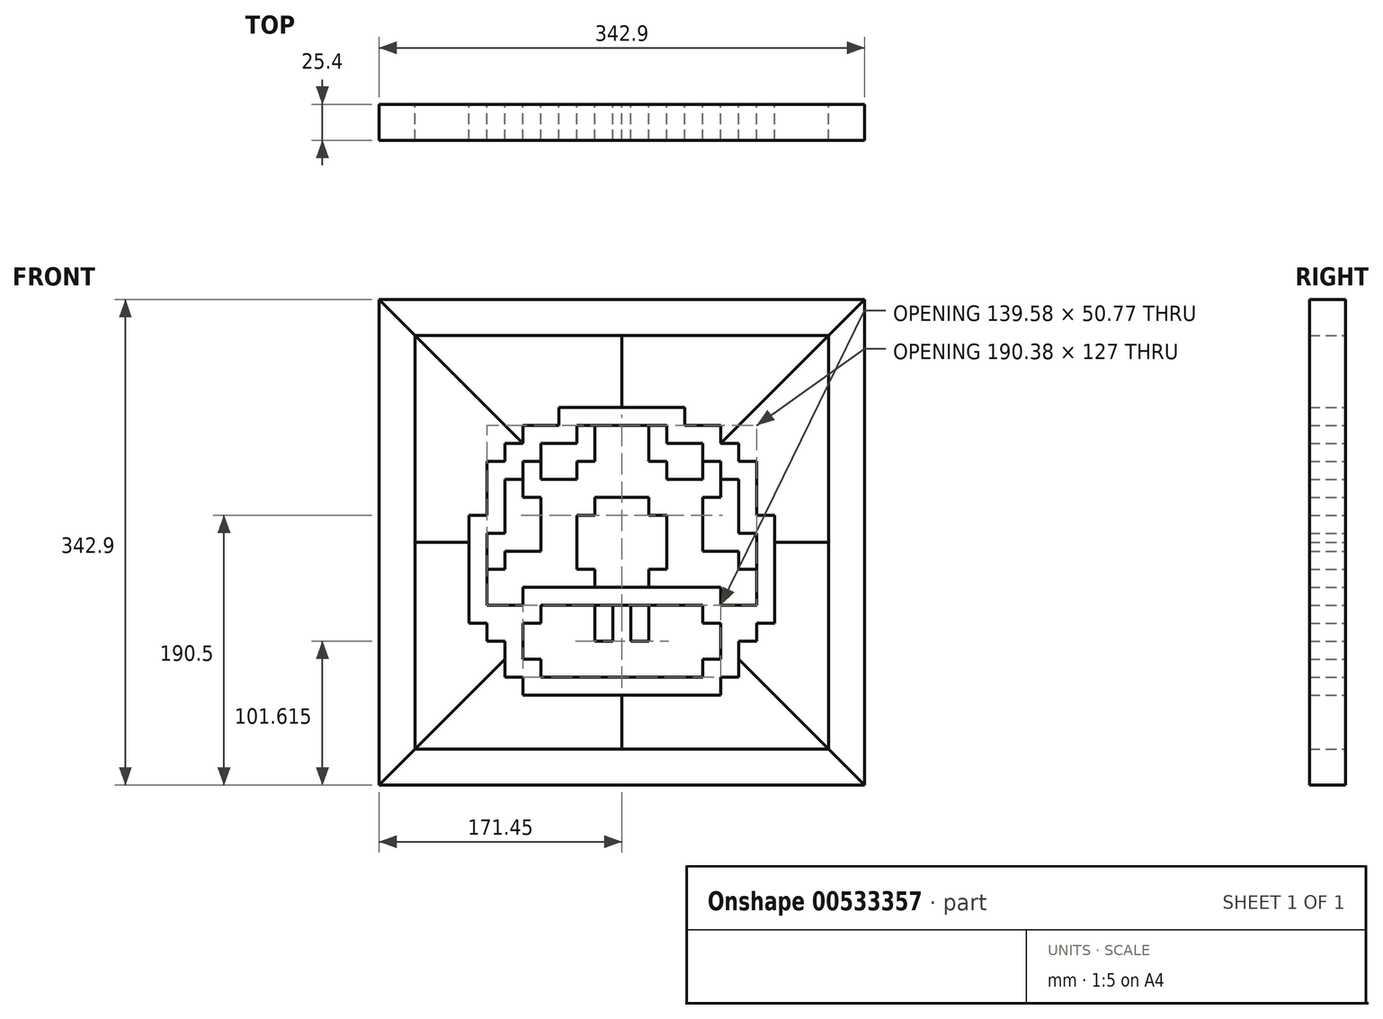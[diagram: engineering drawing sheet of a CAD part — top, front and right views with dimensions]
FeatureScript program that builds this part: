
annotation { "Feature Type Name" : "Feature", "Feature Type Description" : "" }
export const myFeature = defineFeature(function(context is Context, id is Id, definition is map)
    precondition{}
    {
        {
            var Q0;
            Q0=qCreatedBy(makeId("Front.planeOp"),FACE);
            var sketch = newSketch(context, id + "F0", { "sketchPlane" : qUnion([Q0])});
            skLineSegment(sketch, "E0.bottom", {"start": v(-171.45, 171.45) * mm, "end": v(171.45, 171.45) * mm});
            skLineSegment(sketch, "E0.top", {"start": v(-171.45, -171.45) * mm, "end": v(171.45, -171.45) * mm});
            skLineSegment(sketch, "E0.left", {"start": v(-171.45, 171.45) * mm, "end": v(-171.45, -171.45) * mm});
            skLineSegment(sketch, "E0.right", {"start": v(171.45, 171.45) * mm, "end": v(171.45, -171.45) * mm});
            skPoint(sketch, "E0.middle", {"position": v(0, 0) * mm});
            skLineSegment(sketch, "E1.0", {"start": v(-146.05, 146.05) * mm, "end": v(146.05, 146.05) * mm});
            skLineSegment(sketch, "E2.0", {"start": v(146.05, 146.05) * mm, "end": v(146.05, -146.05) * mm});
            skLineSegment(sketch, "E3.0", {"start": v(-146.05, -146.05) * mm, "end": v(146.05, -146.05) * mm});
            skLineSegment(sketch, "E4.0", {"start": v(-146.05, 146.05) * mm, "end": v(-146.05, -146.05) * mm});
            skLineSegment(sketch, "E5", {"start": v(-171.45, 171.45) * mm, "end": v(-146.05, 146.05) * mm});
            skLineSegment(sketch, "E6", {"start": v(171.45, 171.45) * mm, "end": v(146.05, 146.05) * mm});
            skLineSegment(sketch, "E7", {"start": v(171.45, -171.45) * mm, "end": v(146.05, -146.05) * mm});
            skLineSegment(sketch, "E8", {"start": v(-171.45, -171.45) * mm, "end": v(-146.05, -146.05) * mm});
            skLineSegment(sketch, "E9.top", {"start": v(-69.8, -107.92) * mm, "end": v(69.8, -107.92) * mm});
            skLineSegment(sketch, "E10", {"start": v(-69.8, -107.92) * mm, "end": v(-69.8, -95.22) * mm});
            skLineSegment(sketch, "E11", {"start": v(-57.1, -95.22) * mm, "end": v(0, -95.22) * mm});
            skLineSegment(sketch, "E12", {"start": v(-69.8, -95.22) * mm, "end": v(-82.5, -95.22) * mm});
            skLineSegment(sketch, "E13", {"start": v(-82.5, -95.22) * mm, "end": v(-82.5, -82.5) * mm});
            skLineSegment(sketch, "E14", {"start": v(-82.5, -69.82) * mm, "end": v(-95.2, -69.85) * mm});
            skLineSegment(sketch, "E15", {"start": v(-57.1, -82.55) * mm, "end": v(-69.8, -82.55) * mm});
            skLineSegment(sketch, "E16", {"start": v(-69.8, -82.55) * mm, "end": v(-69.8, -57.15) * mm});
            skLineSegment(sketch, "E17", {"start": v(-95.2, -69.85) * mm, "end": v(-95.2, -57.15) * mm});
            skLineSegment(sketch, "E18", {"start": v(-95.2, -57.15) * mm, "end": v(-107.9, -57.15) * mm});
            skLineSegment(sketch, "E19", {"start": v(-69.8, -57.15) * mm, "end": v(-57.1, -57.15) * mm});
            skLineSegment(sketch, "E20", {"start": v(-57.1, -57.15) * mm, "end": v(-57.1, -44.45) * mm});
            skLineSegment(sketch, "E21", {"start": v(-57.1, -44.45) * mm, "end": v(0, -44.45) * mm});
            skLineSegment(sketch, "E22", {"start": v(-107.9, -57.15) * mm, "end": v(-107.9, 19.05) * mm});
            skLineSegment(sketch, "E23", {"start": v(-107.9, 19.05) * mm, "end": v(-95.2, 19.05) * mm});
            skLineSegment(sketch, "E24", {"start": v(-95.2, 19.05) * mm, "end": v(-95.25, 57.15) * mm});
            skLineSegment(sketch, "E25", {"start": v(-95.25, 57.15) * mm, "end": v(-82.55, 57.15) * mm});
            skLineSegment(sketch, "E26", {"start": v(-82.55, 57.15) * mm, "end": v(-82.55, 69.85) * mm});
            skLineSegment(sketch, "E27", {"start": v(-82.55, 69.85) * mm, "end": v(-69.85, 69.85) * mm});
            skLineSegment(sketch, "E28", {"start": v(-69.85, 69.85) * mm, "end": v(-69.85, 82.55) * mm});
            skLineSegment(sketch, "E29", {"start": v(-69.85, 82.55) * mm, "end": v(-44.45, 82.55) * mm});
            skLineSegment(sketch, "E30", {"start": v(-44.45, 82.55) * mm, "end": v(-44.45, 95.25) * mm});
            skLineSegment(sketch, "E31", {"start": v(-44.45, 95.25) * mm, "end": v(0, 95.25) * mm});
            skLineSegment(sketch, "E32", {"start": v(-57.1, -82.55) * mm, "end": v(-57.1, -95.22) * mm});
            skLineSegment(sketch, "E33", {"start": v(-69.8, -44.45) * mm, "end": v(-95.2, -44.45) * mm});
            skLineSegment(sketch, "E34", {"start": v(-95.2, -44.45) * mm, "end": v(-95.2, 6.35) * mm});
            skLineSegment(sketch, "E35", {"start": v(-95.2, 6.35) * mm, "end": v(-82.5, 6.35) * mm});
            skLineSegment(sketch, "E36", {"start": v(-82.5, 6.35) * mm, "end": v(-82.5, 44.45) * mm});
            skLineSegment(sketch, "E37", {"start": v(-82.5, 44.45) * mm, "end": v(-69.8, 44.45) * mm});
            skLineSegment(sketch, "E38", {"start": v(-69.8, 44.45) * mm, "end": v(-69.8, 57.15) * mm});
            skLineSegment(sketch, "E39", {"start": v(-69.8, 57.15) * mm, "end": v(-57.1, 57.15) * mm});
            skLineSegment(sketch, "E40", {"start": v(-57.1, 57.15) * mm, "end": v(-57.1, 69.85) * mm});
            skLineSegment(sketch, "E41", {"start": v(-57.1, 69.85) * mm, "end": v(-31.7, 69.85) * mm});
            skLineSegment(sketch, "E42", {"start": v(-31.7, 69.85) * mm, "end": v(-31.7, 82.55) * mm});
            skLineSegment(sketch, "E43", {"start": v(-31.7, 82.55) * mm, "end": v(0, 82.55) * mm});
            skLineSegment(sketch, "E44", {"start": v(0, 100.28) * mm, "end": v(0, -44.45) * mm, "construction": true});
            skLineSegment(sketch, "E45.MirrorCS", {"start": v(95.2, -69.85) * mm, "end": v(95.2, -57.15) * mm});
            skLineSegment(sketch, "E46.MirrorCS", {"start": v(44.45, 82.55) * mm, "end": v(44.45, 95.25) * mm});
            skLineSegment(sketch, "E47.MirrorCS", {"start": v(82.5, -69.82) * mm, "end": v(95.2, -69.85) * mm});
            skLineSegment(sketch, "E48.MirrorCS", {"start": v(82.5, -95.22) * mm, "end": v(82.5, -69.82) * mm});
            skLineSegment(sketch, "E49.MirrorCS", {"start": v(69.85, 82.55) * mm, "end": v(44.45, 82.55) * mm});
            skLineSegment(sketch, "E50.MirrorCS", {"start": v(82.5, 44.45) * mm, "end": v(69.8, 44.45) * mm});
            skLineSegment(sketch, "E51.MirrorCS", {"start": v(107.9, -57.15) * mm, "end": v(107.9, 19.05) * mm});
            skLineSegment(sketch, "E52.MirrorCS", {"start": v(69.8, -107.92) * mm, "end": v(-69.8, -107.92) * mm});
            skLineSegment(sketch, "E53.MirrorCS", {"start": v(82.55, 57.15) * mm, "end": v(82.55, 69.85) * mm});
            skLineSegment(sketch, "E54.MirrorCS", {"start": v(82.5, 6.35) * mm, "end": v(82.5, 44.45) * mm});
            skLineSegment(sketch, "E55.MirrorCS", {"start": v(57.1, -57.15) * mm, "end": v(57.1, -44.45) * mm});
            skLineSegment(sketch, "E56.MirrorCS", {"start": v(95.2, -57.15) * mm, "end": v(107.9, -57.15) * mm});
            skLineSegment(sketch, "E57.MirrorCS", {"start": v(82.55, 69.85) * mm, "end": v(69.85, 69.85) * mm});
            skLineSegment(sketch, "E58.MirrorCS", {"start": v(31.7, 82.55) * mm, "end": v(0, 82.55) * mm});
            skLineSegment(sketch, "E59.MirrorCS", {"start": v(69.8, 44.45) * mm, "end": v(69.8, 57.15) * mm});
            skLineSegment(sketch, "E60.MirrorCS", {"start": v(57.1, -95.22) * mm, "end": v(0, -95.22) * mm});
            skLineSegment(sketch, "E61.MirrorCS", {"start": v(69.8, -107.92) * mm, "end": v(69.8, -95.22) * mm});
            skLineSegment(sketch, "E62.MirrorCS", {"start": v(69.8, -44.45) * mm, "end": v(95.2, -44.45) * mm});
            skLineSegment(sketch, "E63.MirrorCS", {"start": v(57.1, 57.15) * mm, "end": v(57.1, 69.85) * mm});
            skLineSegment(sketch, "E64.MirrorCS", {"start": v(69.8, -57.15) * mm, "end": v(57.1, -57.15) * mm});
            skLineSegment(sketch, "E65.MirrorCS", {"start": v(95.25, 57.15) * mm, "end": v(82.55, 57.15) * mm});
            skLineSegment(sketch, "E66.MirrorCS", {"start": v(95.2, -44.45) * mm, "end": v(95.2, 6.35) * mm});
            skLineSegment(sketch, "E67.MirrorCS", {"start": v(57.1, -82.55) * mm, "end": v(69.8, -82.55) * mm});
            skLineSegment(sketch, "E68.MirrorCS", {"start": v(69.8, 57.15) * mm, "end": v(57.1, 57.15) * mm});
            skLineSegment(sketch, "E69.MirrorCS", {"start": v(69.8, -95.22) * mm, "end": v(82.5, -95.22) * mm});
            skLineSegment(sketch, "E70.MirrorCS", {"start": v(95.2, 6.35) * mm, "end": v(82.5, 6.35) * mm});
            skLineSegment(sketch, "E71.MirrorCS", {"start": v(107.9, 19.05) * mm, "end": v(95.2, 19.05) * mm});
            skLineSegment(sketch, "E72.MirrorCS", {"start": v(44.45, 95.25) * mm, "end": v(0, 95.25) * mm});
            skLineSegment(sketch, "E73.MirrorCS", {"start": v(57.1, -44.45) * mm, "end": v(0, -44.45) * mm});
            skLineSegment(sketch, "E74.MirrorCS", {"start": v(31.7, 69.85) * mm, "end": v(31.7, 82.55) * mm});
            skLineSegment(sketch, "E75.MirrorCS", {"start": v(57.1, 69.85) * mm, "end": v(31.7, 69.85) * mm});
            skLineSegment(sketch, "E76.MirrorCS", {"start": v(69.85, 69.85) * mm, "end": v(69.85, 82.55) * mm});
            skLineSegment(sketch, "E77.MirrorCS", {"start": v(95.2, 19.05) * mm, "end": v(95.25, 57.15) * mm});
            skLineSegment(sketch, "E78.MirrorCS", {"start": v(69.8, -82.55) * mm, "end": v(69.8, -57.15) * mm});
            skLineSegment(sketch, "E79.MirrorCS", {"start": v(57.1, -82.55) * mm, "end": v(57.1, -95.22) * mm});
            skLineSegment(sketch, "E80", {"start": v(-19.05, -44.45) * mm, "end": v(-19.05, -69.85) * mm});
            skLineSegment(sketch, "E81", {"start": v(-19.05, -69.85) * mm, "end": v(-6.35, -69.85) * mm});
            skLineSegment(sketch, "E82", {"start": v(-6.35, -69.85) * mm, "end": v(-6.35, -44.45) * mm});
            skLineSegment(sketch, "E83.MirrorCS", {"start": v(19.05, -69.85) * mm, "end": v(6.35, -69.85) * mm});
            skLineSegment(sketch, "E84.MirrorCS", {"start": v(19.05, -44.45) * mm, "end": v(19.05, -69.85) * mm});
            skLineSegment(sketch, "E85.MirrorCS", {"start": v(6.35, -69.85) * mm, "end": v(6.35, -44.45) * mm});
            skLineSegment(sketch, "E86", {"start": v(-19.05, -31.75) * mm, "end": v(-19.05, -19.05) * mm});
            skLineSegment(sketch, "E87", {"start": v(-19.05, -19.05) * mm, "end": v(-31.75, -19.05) * mm});
            skLineSegment(sketch, "E88", {"start": v(-31.75, -19.05) * mm, "end": v(-31.75, 19.05) * mm});
            skLineSegment(sketch, "E89", {"start": v(-31.75, 19.05) * mm, "end": v(-19.05, 19.05) * mm});
            skLineSegment(sketch, "E90", {"start": v(-19.05, 19.05) * mm, "end": v(-19.05, 31.75) * mm});
            skLineSegment(sketch, "E91", {"start": v(-19.05, 31.75) * mm, "end": v(19.05, 31.75) * mm});
            skLineSegment(sketch, "E92", {"start": v(19.05, 31.75) * mm, "end": v(19.05, 19.05) * mm});
            skLineSegment(sketch, "E93", {"start": v(19.05, 19.05) * mm, "end": v(31.75, 19.05) * mm});
            skLineSegment(sketch, "E94", {"start": v(31.75, 19.05) * mm, "end": v(31.75, -19.05) * mm});
            skLineSegment(sketch, "E95", {"start": v(31.75, -19.05) * mm, "end": v(19.05, -19.05) * mm});
            skLineSegment(sketch, "E96", {"start": v(19.05, -19.05) * mm, "end": v(19.05, -31.75) * mm});
            skLineSegment(sketch, "E97", {"start": v(-95.2, -19.05) * mm, "end": v(-82.5, -19.05) * mm});
            skLineSegment(sketch, "E98", {"start": v(-82.5, -19.05) * mm, "end": v(-82.5, -6.35) * mm});
            skLineSegment(sketch, "E99", {"start": v(-82.5, -6.35) * mm, "end": v(-57.1, -6.35) * mm});
            skLineSegment(sketch, "E100", {"start": v(-57.1, -6.35) * mm, "end": v(-57.1, 31.75) * mm});
            skLineSegment(sketch, "E101", {"start": v(-57.1, 31.75) * mm, "end": v(-69.8, 31.75) * mm});
            skLineSegment(sketch, "E102", {"start": v(-69.8, 31.75) * mm, "end": v(-69.8, 44.45) * mm});
            skLineSegment(sketch, "E103", {"start": v(-57.1, 57.15) * mm, "end": v(-57.1, 44.45) * mm});
            skLineSegment(sketch, "E104", {"start": v(-57.1, 44.45) * mm, "end": v(-31.7, 44.45) * mm});
            skLineSegment(sketch, "E105", {"start": v(-31.7, 44.45) * mm, "end": v(-31.7, 57.15) * mm});
            skLineSegment(sketch, "E106", {"start": v(-31.7, 57.15) * mm, "end": v(-19, 57.15) * mm});
            skLineSegment(sketch, "E107", {"start": v(-19, 57.15) * mm, "end": v(-19, 82.55) * mm});
            skLineSegment(sketch, "E108.MirrorCS", {"start": v(19, 57.15) * mm, "end": v(19, 82.55) * mm});
            skLineSegment(sketch, "E109.MirrorCS", {"start": v(31.7, 57.15) * mm, "end": v(19, 57.15) * mm});
            skLineSegment(sketch, "E110.MirrorCS", {"start": v(31.7, 44.45) * mm, "end": v(31.7, 57.15) * mm});
            skLineSegment(sketch, "E111.MirrorCS", {"start": v(57.1, 44.45) * mm, "end": v(31.7, 44.45) * mm});
            skLineSegment(sketch, "E112.MirrorCS", {"start": v(57.1, 57.15) * mm, "end": v(57.1, 44.45) * mm});
            skLineSegment(sketch, "E113.MirrorCS", {"start": v(69.8, 31.75) * mm, "end": v(69.8, 44.45) * mm});
            skLineSegment(sketch, "E114.MirrorCS", {"start": v(57.1, -6.35) * mm, "end": v(57.1, 31.75) * mm});
            skLineSegment(sketch, "E115.MirrorCS", {"start": v(82.5, -6.35) * mm, "end": v(57.1, -6.35) * mm});
            skLineSegment(sketch, "E116.MirrorCS", {"start": v(82.5, -19.05) * mm, "end": v(82.5, -6.35) * mm});
            skLineSegment(sketch, "E117.MirrorCS", {"start": v(95.2, -19.05) * mm, "end": v(82.5, -19.05) * mm});
            skLineSegment(sketch, "E118.MirrorCS", {"start": v(57.1, 31.75) * mm, "end": v(69.8, 31.75) * mm});
            skLineSegment(sketch, "E119", {"start": v(-146.05, 146.05) * mm, "end": v(-69.85, 69.85) * mm});
            skLineSegment(sketch, "E120", {"start": v(0, 95.25) * mm, "end": v(0, 146.05) * mm});
            skLineSegment(sketch, "E121", {"start": v(146.05, 146.05) * mm, "end": v(69.85, 69.85) * mm});
            skLineSegment(sketch, "E122", {"start": v(-146.05, -146.05) * mm, "end": v(-82.5, -82.5) * mm});
            skLineSegment(sketch, "E123", {"start": v(-82.5, -82.5) * mm, "end": v(-82.5, -69.82) * mm});
            skLineSegment(sketch, "E124.MirrorCS", {"start": v(146.05, -146.05) * mm, "end": v(82.5, -82.5) * mm});
            skLineSegment(sketch, "E125", {"start": v(-107.9, 0) * mm, "end": v(-146.05, 0) * mm});
            skLineSegment(sketch, "E126.MirrorCS", {"start": v(107.9, 0) * mm, "end": v(146.05, 0) * mm});
            skLineSegment(sketch, "E127", {"start": v(0, -107.92) * mm, "end": v(0, -146.05) * mm});
            skLineSegment(sketch, "E128", {"start": v(-69.8, -44.45) * mm, "end": v(-69.8, -31.75) * mm});
            skLineSegment(sketch, "E129", {"start": v(-69.8, -31.75) * mm, "end": v(69.8, -31.75) * mm});
            skLineSegment(sketch, "E130", {"start": v(69.8, -31.75) * mm, "end": v(69.8, -44.45) * mm});
            skSolve(sketch);
        }
        {
            var Q0;
            Q0=makeQuery(id+"F0.imprint","IMPRINT",FACE,{"disambiguationData":[TD([[makeQuery(id+"F0.imprint","IMPRINT",EDGE,{"derivedFrom":sQuery(id+"F0.wireOp",EDGE,"E0.bottom")}),-1.0]])]});
            var Q1;
            Q1=makeQuery(id+"F0.imprint","IMPRINT",FACE,{"disambiguationData":[TD([[makeQuery(id+"F0.imprint","IMPRINT",EDGE,{"derivedFrom":sQuery(id+"F0.wireOp",EDGE,"E0.top")}),1.0]])]});
            var Q2;
            Q2=makeQuery(id+"F0.imprint","IMPRINT",FACE,{"disambiguationData":[TD([[makeQuery(id+"F0.imprint","IMPRINT",EDGE,{"derivedFrom":sQuery(id+"F0.wireOp",EDGE,"E14")}),1.0]])]});
            var Q3;
            Q3=makeQuery(id+"F0.imprint","IMPRINT",FACE,{"disambiguationData":[TD([[makeQuery(id+"F0.imprint","IMPRINT",EDGE,{"derivedFrom":sQuery(id+"F0.wireOp",EDGE,"E45.MirrorCS")}),-1.0]])]});
            extrude(context, id + "F1", {"entities" : qUnion([Q0, Q1, Q2, Q3]), "depth" : 25.4 * mm, "offsetDistance" : 25.4 * mm});
        }
        {
            var Q0;
            Q0=makeQuery(id+"F0.imprint","IMPRINT",FACE,{"disambiguationData":[TD([[makeQuery(id+"F0.imprint","IMPRINT",EDGE,{"derivedFrom":sQuery(id+"F0.wireOp",EDGE,"E0.left")}),1.0]])]});
            var Q1;
            Q1=makeQuery(id+"F0.imprint","IMPRINT",FACE,{"disambiguationData":[TD([[makeQuery(id+"F0.imprint","IMPRINT",EDGE,{"derivedFrom":sQuery(id+"F0.wireOp",EDGE,"E0.right")}),-1.0]])]});
            var Q2;
            {var subQ3=sQuery(id+"F0.wireOp",EDGE,"E10");Q2=makeQuery(id+"F0.imprint","IMPRINT",FACE,{"disambiguationData":[TD([[makeQuery(id+"F0.imprint","IMPRINT",EDGE,{"derivedFrom":subQ3}),1.0]])]});}
            var Q3;
            {var subQ0=sQuery(id+"F0.wireOp",EDGE,"E86");Q3=makeQuery(id+"F0.imprint","IMPRINT",FACE,{"disambiguationData":[TD([[makeQuery(id+"F0.imprint","IMPRINT",EDGE,{"derivedFrom":subQ0}),-1.0]])]});}
            extrude(context, id + "F2", {"entities" : qUnion([Q0, Q1, Q2, Q3]), "depth" : 25.4 * mm, "offsetDistance" : 25.4 * mm});
        }
        {
            var Q0;
            {var subQ0=sQuery(id+"F0.wireOp",EDGE,"E61.MirrorCS");Q0=makeQuery(id+"F0.imprint","IMPRINT",FACE,{"disambiguationData":[TD([[makeQuery(id+"F0.imprint","IMPRINT",EDGE,{"derivedFrom":subQ0}),-1.0]])]});}
            var Q1;
            {var subQ0=sQuery(id+"F0.wireOp",EDGE,"E23");Q1=makeQuery(id+"F0.imprint","IMPRINT",FACE,{"disambiguationData":[TD([[makeQuery(id+"F0.imprint","IMPRINT",EDGE,{"derivedFrom":subQ0}),1.0]])]});}
            var Q2;
            Q2=makeQuery(id+"F0.imprint","IMPRINT",FACE,{"disambiguationData":[TD([[makeQuery(id+"F0.imprint","IMPRINT",EDGE,{"derivedFrom":sQuery(id+"F0.wireOp",EDGE,"E46.MirrorCS")}),-1.0]])]});
            extrude(context, id + "F3", {"entities" : qUnion([Q0, Q1, Q2]), "depth" : 25.4 * mm, "offsetDistance" : 25.4 * mm});
        }
        {
            var Q0;
            Q0=makeQuery(id+"F0.imprint","IMPRINT",FACE,{"disambiguationData":[TD([[makeQuery(id+"F0.imprint","IMPRINT",EDGE,{"derivedFrom":sQuery(id+"F0.wireOp",EDGE,"E28")}),1.0]])]});
            var Q1;
            Q1=makeQuery(id+"F0.imprint","IMPRINT",FACE,{"disambiguationData":[TD([[makeQuery(id+"F0.imprint","IMPRINT",EDGE,{"derivedFrom":sQuery(id+"F0.wireOp",EDGE,"E53.MirrorCS")}),-1.0]])]});
            var Q2;
            {var subQ1=sQuery(id+"F0.wireOp",EDGE,"E33");Q2=makeQuery(id+"F0.imprint","IMPRINT",FACE,{"disambiguationData":[TD([[makeQuery(id+"F0.imprint","IMPRINT",EDGE,{"derivedFrom":subQ1}),-1.0]])]});}
            extrude(context, id + "F4", {"entities" : qUnion([Q0, Q1, Q2]), "depth" : 25.4 * mm, "offsetDistance" : 25.4 * mm});
        }
        {
            var Q0;
            {var subQ0=sQuery(id+"F0.wireOp",EDGE,"E80");Q0=makeQuery(id+"F0.imprint","IMPRINT",FACE,{"disambiguationData":[TD([[makeQuery(id+"F0.imprint","IMPRINT",EDGE,{"derivedFrom":subQ0}),1.0]])]});}
            var Q1;
            Q1=makeQuery(id+"F0.imprint","IMPRINT",FACE,{"disambiguationData":[TD([[makeQuery(id+"F0.imprint","IMPRINT",EDGE,{"derivedFrom":sQuery(id+"F0.wireOp",EDGE,"E83.MirrorCS")}),-1.0]])]});
            var Q2;
            Q2=makeQuery(id+"F0.imprint","IMPRINT",FACE,{"disambiguationData":[TD([[makeQuery(id+"F0.imprint","IMPRINT",EDGE,{"derivedFrom":sQuery(id+"F0.wireOp",EDGE,"E50.MirrorCS")}),1.0]])]});
            var Q3;
            Q3=makeQuery(id+"F0.imprint","IMPRINT",FACE,{"disambiguationData":[TD([[makeQuery(id+"F0.imprint","IMPRINT",EDGE,{"derivedFrom":sQuery(id+"F0.wireOp",EDGE,"E63.MirrorCS")}),1.0]])]});
            var Q4;
            Q4=makeQuery(id+"F0.imprint","IMPRINT",FACE,{"disambiguationData":[TD([[makeQuery(id+"F0.imprint","IMPRINT",EDGE,{"derivedFrom":sQuery(id+"F0.wireOp",EDGE,"E40")}),-1.0]])]});
            var Q5;
            {var subQ0=sQuery(id+"F0.wireOp",EDGE,"E35");Q5=makeQuery(id+"F0.imprint","IMPRINT",FACE,{"disambiguationData":[TD([[makeQuery(id+"F0.imprint","IMPRINT",EDGE,{"derivedFrom":subQ0}),-1.0]])]});}
            extrude(context, id + "F5", {"entities" : qUnion([Q0, Q1, Q2, Q3, Q4, Q5]), "depth" : 25.4 * mm, "offsetDistance" : 25.4 * mm});
        }
        {
            var Q0;
            Q0=makeQuery(id+"F0.imprint","IMPRINT",FACE,{"disambiguationData":[TD([[makeQuery(id+"F0.imprint","IMPRINT",EDGE,{"derivedFrom":sQuery(id+"F0.wireOp",EDGE,"E11")}),1.0]])]});
            extrude(context, id + "F6", {"entities" : qUnion([Q0]), "depth" : 25.4 * mm, "offsetDistance" : 25.4 * mm});
        }
        {
            var Q0;
            {var subQ18=sQuery(id+"F0.wireOp",EDGE,"E10");Q0=makeQuery(id+"F0.imprint","IMPRINT",FACE,{"disambiguationData":[TD([[makeQuery(id+"F0.imprint","IMPRINT",EDGE,{"derivedFrom":subQ18}),-1.0]])]});}
            extrude(context, id + "F7", {"entities" : qUnion([Q0]), "depth" : 25.4 * mm, "offsetDistance" : 25.4 * mm});
        }
    });
